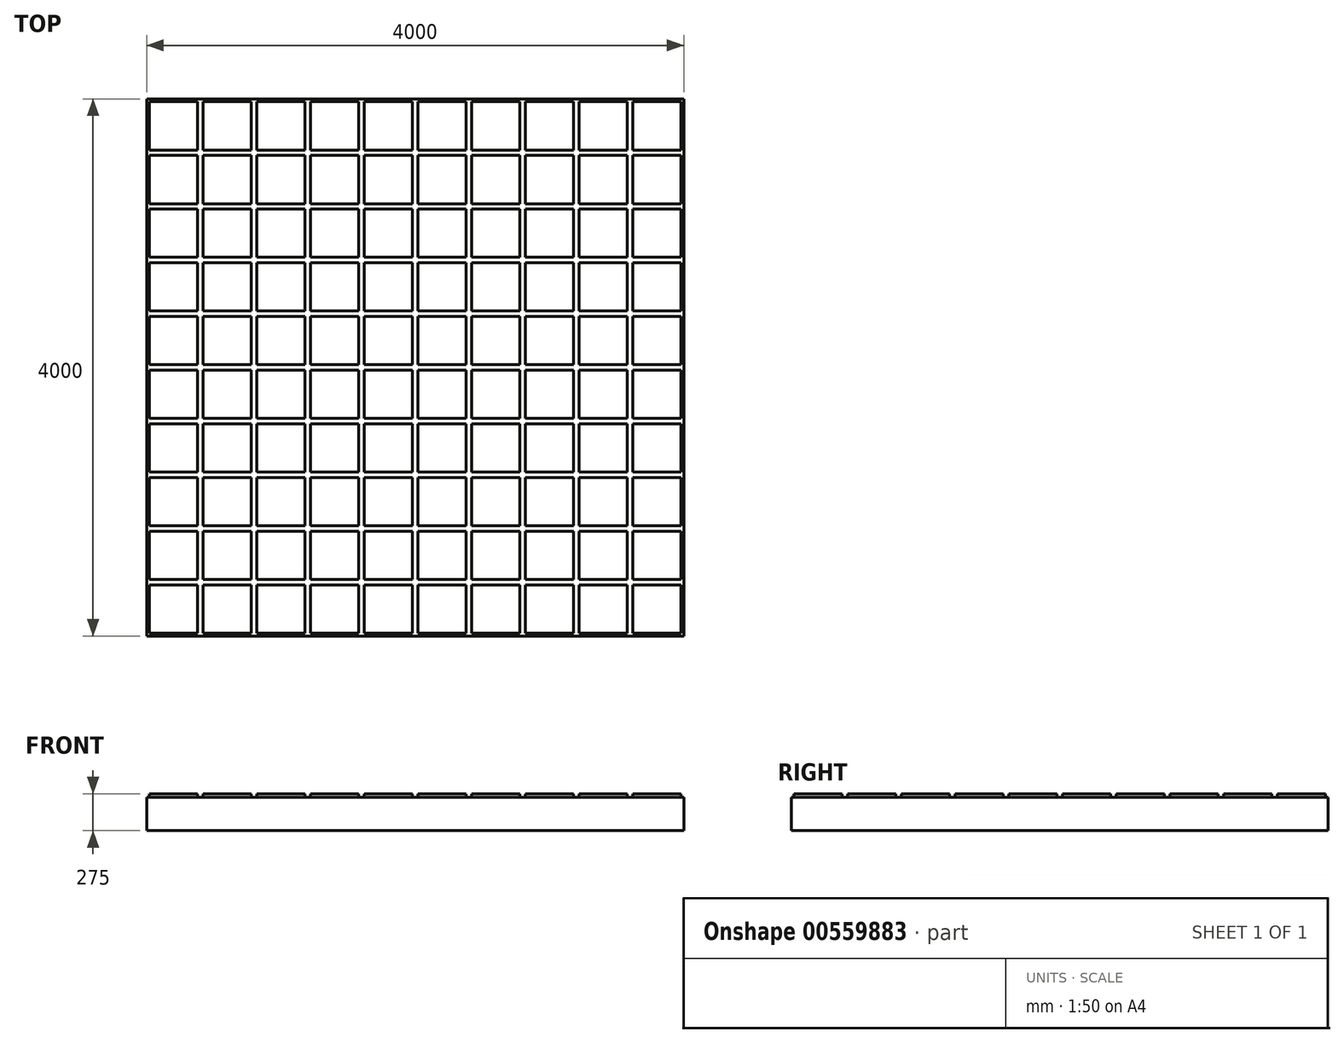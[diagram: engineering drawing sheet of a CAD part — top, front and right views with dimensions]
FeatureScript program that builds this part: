
annotation { "Feature Type Name" : "Feature", "Feature Type Description" : "" }
export const myFeature = defineFeature(function(context is Context, id is Id, definition is map)
    precondition{}
    {
        {
            var Q0;
            Q0=qCreatedBy(makeId("Top.planeOp"),FACE);
            var sketch = newSketch(context, id + "F0", { "sketchPlane" : qUnion([Q0])});
            skLineSegment(sketch, "E0.bottom", {"start": v(2000, 2000) * mm, "end": v(-2000, 2000) * mm});
            skLineSegment(sketch, "E0.top", {"start": v(2000, -2000) * mm, "end": v(-2000, -2000) * mm});
            skLineSegment(sketch, "E0.left", {"start": v(2000, 2000) * mm, "end": v(2000, -2000) * mm});
            skLineSegment(sketch, "E0.right", {"start": v(-2000, 2000) * mm, "end": v(-2000, -2000) * mm});
            skPoint(sketch, "E0.middle", {"position": v(0, 0) * mm});
            skSolve(sketch);
        }
        {
            var Q0;
            Q0 = qSketchRegion(id + "F0", true);
            extrude(context, id + "F1", {"entities" : qUnion([Q0]), "depth" : 250 * mm, "offsetDistance" : 25 * mm});
        }
        {
            var Q0;
            Q0=makeQuery(id+"F1.opExtrude","CAP_FACE",FACE,{"disambiguationData":[OSD([sQuery(id+"F0.wireOp",EDGE,"E0.bottom"),sQuery(id+"F0.wireOp",EDGE,"E0.top"),sQuery(id+"F0.wireOp",EDGE,"E0.left"),sQuery(id+"F0.wireOp",EDGE,"E0.right")])],"isStart":false});
            var sketch = newSketch(context, id + "F2", { "sketchPlane" : qUnion([Q0])});
            skLineSegment(sketch, "E1.bottom", {"start": v(-1620, 1620) * mm, "end": v(-1980, 1620) * mm});
            skLineSegment(sketch, "E1.top", {"start": v(-1620, 1980) * mm, "end": v(-1980, 1980) * mm});
            skLineSegment(sketch, "E1.left", {"start": v(-1620, 1620) * mm, "end": v(-1620, 1980) * mm});
            skLineSegment(sketch, "E1.right", {"start": v(-1980, 1620) * mm, "end": v(-1980, 1980) * mm});
            skPoint(sketch, "E1.middle", {"position": v(-1800, 1800) * mm});
            skLineSegment(sketch, "E2.0.1.0", {"start": v(-1620, 1580) * mm, "end": v(-1980, 1580) * mm});
            skLineSegment(sketch, "E2.0.1.1", {"start": v(-1980, 1220) * mm, "end": v(-1980, 1580) * mm});
            skLineSegment(sketch, "E2.0.1.2", {"start": v(-1620, 1220) * mm, "end": v(-1620, 1580) * mm});
            skLineSegment(sketch, "E2.0.1.3", {"start": v(-1620, 1220) * mm, "end": v(-1980, 1220) * mm});
            skLineSegment(sketch, "E2.0.2.0", {"start": v(-1620, 1180) * mm, "end": v(-1980, 1180) * mm});
            skLineSegment(sketch, "E2.0.2.1", {"start": v(-1980, 820) * mm, "end": v(-1980, 1180) * mm});
            skLineSegment(sketch, "E2.0.2.2", {"start": v(-1620, 820) * mm, "end": v(-1620, 1180) * mm});
            skLineSegment(sketch, "E2.0.2.3", {"start": v(-1620, 820) * mm, "end": v(-1980, 820) * mm});
            skLineSegment(sketch, "E2.0.3.0", {"start": v(-1620, 780) * mm, "end": v(-1980, 780) * mm});
            skLineSegment(sketch, "E2.0.3.1", {"start": v(-1980, 420) * mm, "end": v(-1980, 780) * mm});
            skLineSegment(sketch, "E2.0.3.2", {"start": v(-1620, 420) * mm, "end": v(-1620, 780) * mm});
            skLineSegment(sketch, "E2.0.3.3", {"start": v(-1620, 420) * mm, "end": v(-1980, 420) * mm});
            skLineSegment(sketch, "E2.0.4.0", {"start": v(-1620, 380) * mm, "end": v(-1980, 380) * mm});
            skLineSegment(sketch, "E2.0.4.1", {"start": v(-1980, 20) * mm, "end": v(-1980, 380) * mm});
            skLineSegment(sketch, "E2.0.4.2", {"start": v(-1620, 20) * mm, "end": v(-1620, 380) * mm});
            skLineSegment(sketch, "E2.0.4.3", {"start": v(-1620, 20) * mm, "end": v(-1980, 20) * mm});
            skLineSegment(sketch, "E2.0.5.0", {"start": v(-1620, -20) * mm, "end": v(-1980, -20) * mm});
            skLineSegment(sketch, "E2.0.5.1", {"start": v(-1980, -380) * mm, "end": v(-1980, -20) * mm});
            skLineSegment(sketch, "E2.0.5.2", {"start": v(-1620, -380) * mm, "end": v(-1620, -20) * mm});
            skLineSegment(sketch, "E2.0.5.3", {"start": v(-1620, -380) * mm, "end": v(-1980, -380) * mm});
            skLineSegment(sketch, "E2.0.6.0", {"start": v(-1620, -420) * mm, "end": v(-1980, -420) * mm});
            skLineSegment(sketch, "E2.0.6.1", {"start": v(-1980, -780) * mm, "end": v(-1980, -420) * mm});
            skLineSegment(sketch, "E2.0.6.2", {"start": v(-1620, -780) * mm, "end": v(-1620, -420) * mm});
            skLineSegment(sketch, "E2.0.6.3", {"start": v(-1620, -780) * mm, "end": v(-1980, -780) * mm});
            skLineSegment(sketch, "E2.0.7.0", {"start": v(-1620, -820) * mm, "end": v(-1980, -820) * mm});
            skLineSegment(sketch, "E2.0.7.1", {"start": v(-1980, -1180) * mm, "end": v(-1980, -820) * mm});
            skLineSegment(sketch, "E2.0.7.2", {"start": v(-1620, -1180) * mm, "end": v(-1620, -820) * mm});
            skLineSegment(sketch, "E2.0.7.3", {"start": v(-1620, -1180) * mm, "end": v(-1980, -1180) * mm});
            skLineSegment(sketch, "E2.0.8.0", {"start": v(-1620, -1220) * mm, "end": v(-1980, -1220) * mm});
            skLineSegment(sketch, "E2.0.8.1", {"start": v(-1980, -1580) * mm, "end": v(-1980, -1220) * mm});
            skLineSegment(sketch, "E2.0.8.2", {"start": v(-1620, -1580) * mm, "end": v(-1620, -1220) * mm});
            skLineSegment(sketch, "E2.0.8.3", {"start": v(-1620, -1580) * mm, "end": v(-1980, -1580) * mm});
            skLineSegment(sketch, "E2.0.9.0", {"start": v(-1620, -1620) * mm, "end": v(-1980, -1620) * mm});
            skLineSegment(sketch, "E2.0.9.1", {"start": v(-1980, -1980) * mm, "end": v(-1980, -1620) * mm});
            skLineSegment(sketch, "E2.0.9.2", {"start": v(-1620, -1980) * mm, "end": v(-1620, -1620) * mm});
            skLineSegment(sketch, "E2.0.9.3", {"start": v(-1620, -1980) * mm, "end": v(-1980, -1980) * mm});
            skLineSegment(sketch, "E2.1.0.0", {"start": v(-1220, 1980) * mm, "end": v(-1580, 1980) * mm});
            skLineSegment(sketch, "E2.1.0.1", {"start": v(-1580, 1620) * mm, "end": v(-1580, 1980) * mm});
            skLineSegment(sketch, "E2.1.0.2", {"start": v(-1220, 1620) * mm, "end": v(-1220, 1980) * mm});
            skLineSegment(sketch, "E2.1.0.3", {"start": v(-1220, 1620) * mm, "end": v(-1580, 1620) * mm});
            skLineSegment(sketch, "E2.1.1.0", {"start": v(-1220, 1580) * mm, "end": v(-1580, 1580) * mm});
            skLineSegment(sketch, "E2.1.1.1", {"start": v(-1580, 1220) * mm, "end": v(-1580, 1580) * mm});
            skLineSegment(sketch, "E2.1.1.2", {"start": v(-1220, 1220) * mm, "end": v(-1220, 1580) * mm});
            skLineSegment(sketch, "E2.1.1.3", {"start": v(-1220, 1220) * mm, "end": v(-1580, 1220) * mm});
            skLineSegment(sketch, "E2.1.2.0", {"start": v(-1220, 1180) * mm, "end": v(-1580, 1180) * mm});
            skLineSegment(sketch, "E2.1.2.1", {"start": v(-1580, 820) * mm, "end": v(-1580, 1180) * mm});
            skLineSegment(sketch, "E2.1.2.2", {"start": v(-1220, 820) * mm, "end": v(-1220, 1180) * mm});
            skLineSegment(sketch, "E2.1.2.3", {"start": v(-1220, 820) * mm, "end": v(-1580, 820) * mm});
            skLineSegment(sketch, "E2.1.3.0", {"start": v(-1220, 780) * mm, "end": v(-1580, 780) * mm});
            skLineSegment(sketch, "E2.1.3.1", {"start": v(-1580, 420) * mm, "end": v(-1580, 780) * mm});
            skLineSegment(sketch, "E2.1.3.2", {"start": v(-1220, 420) * mm, "end": v(-1220, 780) * mm});
            skLineSegment(sketch, "E2.1.3.3", {"start": v(-1220, 420) * mm, "end": v(-1580, 420) * mm});
            skLineSegment(sketch, "E2.1.4.0", {"start": v(-1220, 380) * mm, "end": v(-1580, 380) * mm});
            skLineSegment(sketch, "E2.1.4.1", {"start": v(-1580, 20) * mm, "end": v(-1580, 380) * mm});
            skLineSegment(sketch, "E2.1.4.2", {"start": v(-1220, 20) * mm, "end": v(-1220, 380) * mm});
            skLineSegment(sketch, "E2.1.4.3", {"start": v(-1220, 20) * mm, "end": v(-1580, 20) * mm});
            skLineSegment(sketch, "E2.1.5.0", {"start": v(-1220, -20) * mm, "end": v(-1580, -20) * mm});
            skLineSegment(sketch, "E2.1.5.1", {"start": v(-1580, -380) * mm, "end": v(-1580, -20) * mm});
            skLineSegment(sketch, "E2.1.5.2", {"start": v(-1220, -380) * mm, "end": v(-1220, -20) * mm});
            skLineSegment(sketch, "E2.1.5.3", {"start": v(-1220, -380) * mm, "end": v(-1580, -380) * mm});
            skLineSegment(sketch, "E2.1.6.0", {"start": v(-1220, -420) * mm, "end": v(-1580, -420) * mm});
            skLineSegment(sketch, "E2.1.6.1", {"start": v(-1580, -780) * mm, "end": v(-1580, -420) * mm});
            skLineSegment(sketch, "E2.1.6.2", {"start": v(-1220, -780) * mm, "end": v(-1220, -420) * mm});
            skLineSegment(sketch, "E2.1.6.3", {"start": v(-1220, -780) * mm, "end": v(-1580, -780) * mm});
            skLineSegment(sketch, "E2.1.7.0", {"start": v(-1220, -820) * mm, "end": v(-1580, -820) * mm});
            skLineSegment(sketch, "E2.1.7.1", {"start": v(-1580, -1180) * mm, "end": v(-1580, -820) * mm});
            skLineSegment(sketch, "E2.1.7.2", {"start": v(-1220, -1180) * mm, "end": v(-1220, -820) * mm});
            skLineSegment(sketch, "E2.1.7.3", {"start": v(-1220, -1180) * mm, "end": v(-1580, -1180) * mm});
            skLineSegment(sketch, "E2.1.8.0", {"start": v(-1220, -1220) * mm, "end": v(-1580, -1220) * mm});
            skLineSegment(sketch, "E2.1.8.1", {"start": v(-1580, -1580) * mm, "end": v(-1580, -1220) * mm});
            skLineSegment(sketch, "E2.1.8.2", {"start": v(-1220, -1580) * mm, "end": v(-1220, -1220) * mm});
            skLineSegment(sketch, "E2.1.8.3", {"start": v(-1220, -1580) * mm, "end": v(-1580, -1580) * mm});
            skLineSegment(sketch, "E2.1.9.0", {"start": v(-1220, -1620) * mm, "end": v(-1580, -1620) * mm});
            skLineSegment(sketch, "E2.1.9.1", {"start": v(-1580, -1980) * mm, "end": v(-1580, -1620) * mm});
            skLineSegment(sketch, "E2.1.9.2", {"start": v(-1220, -1980) * mm, "end": v(-1220, -1620) * mm});
            skLineSegment(sketch, "E2.1.9.3", {"start": v(-1220, -1980) * mm, "end": v(-1580, -1980) * mm});
            skLineSegment(sketch, "E2.2.0.0", {"start": v(-820, 1980) * mm, "end": v(-1180, 1980) * mm});
            skLineSegment(sketch, "E2.2.0.1", {"start": v(-1180, 1620) * mm, "end": v(-1180, 1980) * mm});
            skLineSegment(sketch, "E2.2.0.2", {"start": v(-820, 1620) * mm, "end": v(-820, 1980) * mm});
            skLineSegment(sketch, "E2.2.0.3", {"start": v(-820, 1620) * mm, "end": v(-1180, 1620) * mm});
            skLineSegment(sketch, "E2.2.1.0", {"start": v(-820, 1580) * mm, "end": v(-1180, 1580) * mm});
            skLineSegment(sketch, "E2.2.1.1", {"start": v(-1180, 1220) * mm, "end": v(-1180, 1580) * mm});
            skLineSegment(sketch, "E2.2.1.2", {"start": v(-820, 1220) * mm, "end": v(-820, 1580) * mm});
            skLineSegment(sketch, "E2.2.1.3", {"start": v(-820, 1220) * mm, "end": v(-1180, 1220) * mm});
            skLineSegment(sketch, "E2.2.2.0", {"start": v(-820, 1180) * mm, "end": v(-1180, 1180) * mm});
            skLineSegment(sketch, "E2.2.2.1", {"start": v(-1180, 820) * mm, "end": v(-1180, 1180) * mm});
            skLineSegment(sketch, "E2.2.2.2", {"start": v(-820, 820) * mm, "end": v(-820, 1180) * mm});
            skLineSegment(sketch, "E2.2.2.3", {"start": v(-820, 820) * mm, "end": v(-1180, 820) * mm});
            skLineSegment(sketch, "E2.2.3.0", {"start": v(-820, 780) * mm, "end": v(-1180, 780) * mm});
            skLineSegment(sketch, "E2.2.3.1", {"start": v(-1180, 420) * mm, "end": v(-1180, 780) * mm});
            skLineSegment(sketch, "E2.2.3.2", {"start": v(-820, 420) * mm, "end": v(-820, 780) * mm});
            skLineSegment(sketch, "E2.2.3.3", {"start": v(-820, 420) * mm, "end": v(-1180, 420) * mm});
            skLineSegment(sketch, "E2.2.4.0", {"start": v(-820, 380) * mm, "end": v(-1180, 380) * mm});
            skLineSegment(sketch, "E2.2.4.1", {"start": v(-1180, 20) * mm, "end": v(-1180, 380) * mm});
            skLineSegment(sketch, "E2.2.4.2", {"start": v(-820, 20) * mm, "end": v(-820, 380) * mm});
            skLineSegment(sketch, "E2.2.4.3", {"start": v(-820, 20) * mm, "end": v(-1180, 20) * mm});
            skLineSegment(sketch, "E2.2.5.0", {"start": v(-820, -20) * mm, "end": v(-1180, -20) * mm});
            skLineSegment(sketch, "E2.2.5.1", {"start": v(-1180, -380) * mm, "end": v(-1180, -20) * mm});
            skLineSegment(sketch, "E2.2.5.2", {"start": v(-820, -380) * mm, "end": v(-820, -20) * mm});
            skLineSegment(sketch, "E2.2.5.3", {"start": v(-820, -380) * mm, "end": v(-1180, -380) * mm});
            skLineSegment(sketch, "E2.2.6.0", {"start": v(-820, -420) * mm, "end": v(-1180, -420) * mm});
            skLineSegment(sketch, "E2.2.6.1", {"start": v(-1180, -780) * mm, "end": v(-1180, -420) * mm});
            skLineSegment(sketch, "E2.2.6.2", {"start": v(-820, -780) * mm, "end": v(-820, -420) * mm});
            skLineSegment(sketch, "E2.2.6.3", {"start": v(-820, -780) * mm, "end": v(-1180, -780) * mm});
            skLineSegment(sketch, "E2.2.7.0", {"start": v(-820, -820) * mm, "end": v(-1180, -820) * mm});
            skLineSegment(sketch, "E2.2.7.1", {"start": v(-1180, -1180) * mm, "end": v(-1180, -820) * mm});
            skLineSegment(sketch, "E2.2.7.2", {"start": v(-820, -1180) * mm, "end": v(-820, -820) * mm});
            skLineSegment(sketch, "E2.2.7.3", {"start": v(-820, -1180) * mm, "end": v(-1180, -1180) * mm});
            skLineSegment(sketch, "E2.2.8.0", {"start": v(-820, -1220) * mm, "end": v(-1180, -1220) * mm});
            skLineSegment(sketch, "E2.2.8.1", {"start": v(-1180, -1580) * mm, "end": v(-1180, -1220) * mm});
            skLineSegment(sketch, "E2.2.8.2", {"start": v(-820, -1580) * mm, "end": v(-820, -1220) * mm});
            skLineSegment(sketch, "E2.2.8.3", {"start": v(-820, -1580) * mm, "end": v(-1180, -1580) * mm});
            skLineSegment(sketch, "E2.2.9.0", {"start": v(-820, -1620) * mm, "end": v(-1180, -1620) * mm});
            skLineSegment(sketch, "E2.2.9.1", {"start": v(-1180, -1980) * mm, "end": v(-1180, -1620) * mm});
            skLineSegment(sketch, "E2.2.9.2", {"start": v(-820, -1980) * mm, "end": v(-820, -1620) * mm});
            skLineSegment(sketch, "E2.2.9.3", {"start": v(-820, -1980) * mm, "end": v(-1180, -1980) * mm});
            skLineSegment(sketch, "E2.3.0.0", {"start": v(-420, 1980) * mm, "end": v(-780, 1980) * mm});
            skLineSegment(sketch, "E2.3.0.1", {"start": v(-780, 1620) * mm, "end": v(-780, 1980) * mm});
            skLineSegment(sketch, "E2.3.0.2", {"start": v(-420, 1620) * mm, "end": v(-420, 1980) * mm});
            skLineSegment(sketch, "E2.3.0.3", {"start": v(-420, 1620) * mm, "end": v(-780, 1620) * mm});
            skLineSegment(sketch, "E2.3.1.0", {"start": v(-420, 1580) * mm, "end": v(-780, 1580) * mm});
            skLineSegment(sketch, "E2.3.1.1", {"start": v(-780, 1220) * mm, "end": v(-780, 1580) * mm});
            skLineSegment(sketch, "E2.3.1.2", {"start": v(-420, 1220) * mm, "end": v(-420, 1580) * mm});
            skLineSegment(sketch, "E2.3.1.3", {"start": v(-420, 1220) * mm, "end": v(-780, 1220) * mm});
            skLineSegment(sketch, "E2.3.2.0", {"start": v(-420, 1180) * mm, "end": v(-780, 1180) * mm});
            skLineSegment(sketch, "E2.3.2.1", {"start": v(-780, 820) * mm, "end": v(-780, 1180) * mm});
            skLineSegment(sketch, "E2.3.2.2", {"start": v(-420, 820) * mm, "end": v(-420, 1180) * mm});
            skLineSegment(sketch, "E2.3.2.3", {"start": v(-420, 820) * mm, "end": v(-780, 820) * mm});
            skLineSegment(sketch, "E2.3.3.0", {"start": v(-420, 780) * mm, "end": v(-780, 780) * mm});
            skLineSegment(sketch, "E2.3.3.1", {"start": v(-780, 420) * mm, "end": v(-780, 780) * mm});
            skLineSegment(sketch, "E2.3.3.2", {"start": v(-420, 420) * mm, "end": v(-420, 780) * mm});
            skLineSegment(sketch, "E2.3.3.3", {"start": v(-420, 420) * mm, "end": v(-780, 420) * mm});
            skLineSegment(sketch, "E2.3.4.0", {"start": v(-420, 380) * mm, "end": v(-780, 380) * mm});
            skLineSegment(sketch, "E2.3.4.1", {"start": v(-780, 20) * mm, "end": v(-780, 380) * mm});
            skLineSegment(sketch, "E2.3.4.2", {"start": v(-420, 20) * mm, "end": v(-420, 380) * mm});
            skLineSegment(sketch, "E2.3.4.3", {"start": v(-420, 20) * mm, "end": v(-780, 20) * mm});
            skLineSegment(sketch, "E2.3.5.0", {"start": v(-420, -20) * mm, "end": v(-780, -20) * mm});
            skLineSegment(sketch, "E2.3.5.1", {"start": v(-780, -380) * mm, "end": v(-780, -20) * mm});
            skLineSegment(sketch, "E2.3.5.2", {"start": v(-420, -380) * mm, "end": v(-420, -20) * mm});
            skLineSegment(sketch, "E2.3.5.3", {"start": v(-420, -380) * mm, "end": v(-780, -380) * mm});
            skLineSegment(sketch, "E2.3.6.0", {"start": v(-420, -420) * mm, "end": v(-780, -420) * mm});
            skLineSegment(sketch, "E2.3.6.1", {"start": v(-780, -780) * mm, "end": v(-780, -420) * mm});
            skLineSegment(sketch, "E2.3.6.2", {"start": v(-420, -780) * mm, "end": v(-420, -420) * mm});
            skLineSegment(sketch, "E2.3.6.3", {"start": v(-420, -780) * mm, "end": v(-780, -780) * mm});
            skLineSegment(sketch, "E2.3.7.0", {"start": v(-420, -820) * mm, "end": v(-780, -820) * mm});
            skLineSegment(sketch, "E2.3.7.1", {"start": v(-780, -1180) * mm, "end": v(-780, -820) * mm});
            skLineSegment(sketch, "E2.3.7.2", {"start": v(-420, -1180) * mm, "end": v(-420, -820) * mm});
            skLineSegment(sketch, "E2.3.7.3", {"start": v(-420, -1180) * mm, "end": v(-780, -1180) * mm});
            skLineSegment(sketch, "E2.3.8.0", {"start": v(-420, -1220) * mm, "end": v(-780, -1220) * mm});
            skLineSegment(sketch, "E2.3.8.1", {"start": v(-780, -1580) * mm, "end": v(-780, -1220) * mm});
            skLineSegment(sketch, "E2.3.8.2", {"start": v(-420, -1580) * mm, "end": v(-420, -1220) * mm});
            skLineSegment(sketch, "E2.3.8.3", {"start": v(-420, -1580) * mm, "end": v(-780, -1580) * mm});
            skLineSegment(sketch, "E2.3.9.0", {"start": v(-420, -1620) * mm, "end": v(-780, -1620) * mm});
            skLineSegment(sketch, "E2.3.9.1", {"start": v(-780, -1980) * mm, "end": v(-780, -1620) * mm});
            skLineSegment(sketch, "E2.3.9.2", {"start": v(-420, -1980) * mm, "end": v(-420, -1620) * mm});
            skLineSegment(sketch, "E2.3.9.3", {"start": v(-420, -1980) * mm, "end": v(-780, -1980) * mm});
            skLineSegment(sketch, "E2.4.0.0", {"start": v(-20, 1980) * mm, "end": v(-380, 1980) * mm});
            skLineSegment(sketch, "E2.4.0.1", {"start": v(-380, 1620) * mm, "end": v(-380, 1980) * mm});
            skLineSegment(sketch, "E2.4.0.2", {"start": v(-20, 1620) * mm, "end": v(-20, 1980) * mm});
            skLineSegment(sketch, "E2.4.0.3", {"start": v(-20, 1620) * mm, "end": v(-380, 1620) * mm});
            skLineSegment(sketch, "E2.4.1.0", {"start": v(-20, 1580) * mm, "end": v(-380, 1580) * mm});
            skLineSegment(sketch, "E2.4.1.1", {"start": v(-380, 1220) * mm, "end": v(-380, 1580) * mm});
            skLineSegment(sketch, "E2.4.1.2", {"start": v(-20, 1220) * mm, "end": v(-20, 1580) * mm});
            skLineSegment(sketch, "E2.4.1.3", {"start": v(-20, 1220) * mm, "end": v(-380, 1220) * mm});
            skLineSegment(sketch, "E2.4.2.0", {"start": v(-20, 1180) * mm, "end": v(-380, 1180) * mm});
            skLineSegment(sketch, "E2.4.2.1", {"start": v(-380, 820) * mm, "end": v(-380, 1180) * mm});
            skLineSegment(sketch, "E2.4.2.2", {"start": v(-20, 820) * mm, "end": v(-20, 1180) * mm});
            skLineSegment(sketch, "E2.4.2.3", {"start": v(-20, 820) * mm, "end": v(-380, 820) * mm});
            skLineSegment(sketch, "E2.4.3.0", {"start": v(-20, 780) * mm, "end": v(-380, 780) * mm});
            skLineSegment(sketch, "E2.4.3.1", {"start": v(-380, 420) * mm, "end": v(-380, 780) * mm});
            skLineSegment(sketch, "E2.4.3.2", {"start": v(-20, 420) * mm, "end": v(-20, 780) * mm});
            skLineSegment(sketch, "E2.4.3.3", {"start": v(-20, 420) * mm, "end": v(-380, 420) * mm});
            skLineSegment(sketch, "E2.4.4.0", {"start": v(-20, 380) * mm, "end": v(-380, 380) * mm});
            skLineSegment(sketch, "E2.4.4.1", {"start": v(-380, 20) * mm, "end": v(-380, 380) * mm});
            skLineSegment(sketch, "E2.4.4.2", {"start": v(-20, 20) * mm, "end": v(-20, 380) * mm});
            skLineSegment(sketch, "E2.4.4.3", {"start": v(-20, 20) * mm, "end": v(-380, 20) * mm});
            skLineSegment(sketch, "E2.4.5.0", {"start": v(-20, -20) * mm, "end": v(-380, -20) * mm});
            skLineSegment(sketch, "E2.4.5.1", {"start": v(-380, -380) * mm, "end": v(-380, -20) * mm});
            skLineSegment(sketch, "E2.4.5.2", {"start": v(-20, -380) * mm, "end": v(-20, -20) * mm});
            skLineSegment(sketch, "E2.4.5.3", {"start": v(-20, -380) * mm, "end": v(-380, -380) * mm});
            skLineSegment(sketch, "E2.4.6.0", {"start": v(-20, -420) * mm, "end": v(-380, -420) * mm});
            skLineSegment(sketch, "E2.4.6.1", {"start": v(-380, -780) * mm, "end": v(-380, -420) * mm});
            skLineSegment(sketch, "E2.4.6.2", {"start": v(-20, -780) * mm, "end": v(-20, -420) * mm});
            skLineSegment(sketch, "E2.4.6.3", {"start": v(-20, -780) * mm, "end": v(-380, -780) * mm});
            skLineSegment(sketch, "E2.4.7.0", {"start": v(-20, -820) * mm, "end": v(-380, -820) * mm});
            skLineSegment(sketch, "E2.4.7.1", {"start": v(-380, -1180) * mm, "end": v(-380, -820) * mm});
            skLineSegment(sketch, "E2.4.7.2", {"start": v(-20, -1180) * mm, "end": v(-20, -820) * mm});
            skLineSegment(sketch, "E2.4.7.3", {"start": v(-20, -1180) * mm, "end": v(-380, -1180) * mm});
            skLineSegment(sketch, "E2.4.8.0", {"start": v(-20, -1220) * mm, "end": v(-380, -1220) * mm});
            skLineSegment(sketch, "E2.4.8.1", {"start": v(-380, -1580) * mm, "end": v(-380, -1220) * mm});
            skLineSegment(sketch, "E2.4.8.2", {"start": v(-20, -1580) * mm, "end": v(-20, -1220) * mm});
            skLineSegment(sketch, "E2.4.8.3", {"start": v(-20, -1580) * mm, "end": v(-380, -1580) * mm});
            skLineSegment(sketch, "E2.4.9.0", {"start": v(-20, -1620) * mm, "end": v(-380, -1620) * mm});
            skLineSegment(sketch, "E2.4.9.1", {"start": v(-380, -1980) * mm, "end": v(-380, -1620) * mm});
            skLineSegment(sketch, "E2.4.9.2", {"start": v(-20, -1980) * mm, "end": v(-20, -1620) * mm});
            skLineSegment(sketch, "E2.4.9.3", {"start": v(-20, -1980) * mm, "end": v(-380, -1980) * mm});
            skLineSegment(sketch, "E2.5.0.0", {"start": v(380, 1980) * mm, "end": v(20, 1980) * mm});
            skLineSegment(sketch, "E2.5.0.1", {"start": v(20, 1620) * mm, "end": v(20, 1980) * mm});
            skLineSegment(sketch, "E2.5.0.2", {"start": v(380, 1620) * mm, "end": v(380, 1980) * mm});
            skLineSegment(sketch, "E2.5.0.3", {"start": v(380, 1620) * mm, "end": v(20, 1620) * mm});
            skLineSegment(sketch, "E2.5.1.0", {"start": v(380, 1580) * mm, "end": v(20, 1580) * mm});
            skLineSegment(sketch, "E2.5.1.1", {"start": v(20, 1220) * mm, "end": v(20, 1580) * mm});
            skLineSegment(sketch, "E2.5.1.2", {"start": v(380, 1220) * mm, "end": v(380, 1580) * mm});
            skLineSegment(sketch, "E2.5.1.3", {"start": v(380, 1220) * mm, "end": v(20, 1220) * mm});
            skLineSegment(sketch, "E2.5.2.0", {"start": v(380, 1180) * mm, "end": v(20, 1180) * mm});
            skLineSegment(sketch, "E2.5.2.1", {"start": v(20, 820) * mm, "end": v(20, 1180) * mm});
            skLineSegment(sketch, "E2.5.2.2", {"start": v(380, 820) * mm, "end": v(380, 1180) * mm});
            skLineSegment(sketch, "E2.5.2.3", {"start": v(380, 820) * mm, "end": v(20, 820) * mm});
            skLineSegment(sketch, "E2.5.3.0", {"start": v(380, 780) * mm, "end": v(20, 780) * mm});
            skLineSegment(sketch, "E2.5.3.1", {"start": v(20, 420) * mm, "end": v(20, 780) * mm});
            skLineSegment(sketch, "E2.5.3.2", {"start": v(380, 420) * mm, "end": v(380, 780) * mm});
            skLineSegment(sketch, "E2.5.3.3", {"start": v(380, 420) * mm, "end": v(20, 420) * mm});
            skLineSegment(sketch, "E2.5.4.0", {"start": v(380, 380) * mm, "end": v(20, 380) * mm});
            skLineSegment(sketch, "E2.5.4.1", {"start": v(20, 20) * mm, "end": v(20, 380) * mm});
            skLineSegment(sketch, "E2.5.4.2", {"start": v(380, 20) * mm, "end": v(380, 380) * mm});
            skLineSegment(sketch, "E2.5.4.3", {"start": v(380, 20) * mm, "end": v(20, 20) * mm});
            skLineSegment(sketch, "E2.5.5.0", {"start": v(380, -20) * mm, "end": v(20, -20) * mm});
            skLineSegment(sketch, "E2.5.5.1", {"start": v(20, -380) * mm, "end": v(20, -20) * mm});
            skLineSegment(sketch, "E2.5.5.2", {"start": v(380, -380) * mm, "end": v(380, -20) * mm});
            skLineSegment(sketch, "E2.5.5.3", {"start": v(380, -380) * mm, "end": v(20, -380) * mm});
            skLineSegment(sketch, "E2.5.6.0", {"start": v(380, -420) * mm, "end": v(20, -420) * mm});
            skLineSegment(sketch, "E2.5.6.1", {"start": v(20, -780) * mm, "end": v(20, -420) * mm});
            skLineSegment(sketch, "E2.5.6.2", {"start": v(380, -780) * mm, "end": v(380, -420) * mm});
            skLineSegment(sketch, "E2.5.6.3", {"start": v(380, -780) * mm, "end": v(20, -780) * mm});
            skLineSegment(sketch, "E2.5.7.0", {"start": v(380, -820) * mm, "end": v(20, -820) * mm});
            skLineSegment(sketch, "E2.5.7.1", {"start": v(20, -1180) * mm, "end": v(20, -820) * mm});
            skLineSegment(sketch, "E2.5.7.2", {"start": v(380, -1180) * mm, "end": v(380, -820) * mm});
            skLineSegment(sketch, "E2.5.7.3", {"start": v(380, -1180) * mm, "end": v(20, -1180) * mm});
            skLineSegment(sketch, "E2.5.8.0", {"start": v(380, -1220) * mm, "end": v(20, -1220) * mm});
            skLineSegment(sketch, "E2.5.8.1", {"start": v(20, -1580) * mm, "end": v(20, -1220) * mm});
            skLineSegment(sketch, "E2.5.8.2", {"start": v(380, -1580) * mm, "end": v(380, -1220) * mm});
            skLineSegment(sketch, "E2.5.8.3", {"start": v(380, -1580) * mm, "end": v(20, -1580) * mm});
            skLineSegment(sketch, "E2.5.9.0", {"start": v(380, -1620) * mm, "end": v(20, -1620) * mm});
            skLineSegment(sketch, "E2.5.9.1", {"start": v(20, -1980) * mm, "end": v(20, -1620) * mm});
            skLineSegment(sketch, "E2.5.9.2", {"start": v(380, -1980) * mm, "end": v(380, -1620) * mm});
            skLineSegment(sketch, "E2.5.9.3", {"start": v(380, -1980) * mm, "end": v(20, -1980) * mm});
            skLineSegment(sketch, "E2.6.0.0", {"start": v(780, 1980) * mm, "end": v(420, 1980) * mm});
            skLineSegment(sketch, "E2.6.0.1", {"start": v(420, 1620) * mm, "end": v(420, 1980) * mm});
            skLineSegment(sketch, "E2.6.0.2", {"start": v(780, 1620) * mm, "end": v(780, 1980) * mm});
            skLineSegment(sketch, "E2.6.0.3", {"start": v(780, 1620) * mm, "end": v(420, 1620) * mm});
            skLineSegment(sketch, "E2.6.1.0", {"start": v(780, 1580) * mm, "end": v(420, 1580) * mm});
            skLineSegment(sketch, "E2.6.1.1", {"start": v(420, 1220) * mm, "end": v(420, 1580) * mm});
            skLineSegment(sketch, "E2.6.1.2", {"start": v(780, 1220) * mm, "end": v(780, 1580) * mm});
            skLineSegment(sketch, "E2.6.1.3", {"start": v(780, 1220) * mm, "end": v(420, 1220) * mm});
            skLineSegment(sketch, "E2.6.2.0", {"start": v(780, 1180) * mm, "end": v(420, 1180) * mm});
            skLineSegment(sketch, "E2.6.2.1", {"start": v(420, 820) * mm, "end": v(420, 1180) * mm});
            skLineSegment(sketch, "E2.6.2.2", {"start": v(780, 820) * mm, "end": v(780, 1180) * mm});
            skLineSegment(sketch, "E2.6.2.3", {"start": v(780, 820) * mm, "end": v(420, 820) * mm});
            skLineSegment(sketch, "E2.6.3.0", {"start": v(780, 780) * mm, "end": v(420, 780) * mm});
            skLineSegment(sketch, "E2.6.3.1", {"start": v(420, 420) * mm, "end": v(420, 780) * mm});
            skLineSegment(sketch, "E2.6.3.2", {"start": v(780, 420) * mm, "end": v(780, 780) * mm});
            skLineSegment(sketch, "E2.6.3.3", {"start": v(780, 420) * mm, "end": v(420, 420) * mm});
            skLineSegment(sketch, "E2.6.4.0", {"start": v(780, 380) * mm, "end": v(420, 380) * mm});
            skLineSegment(sketch, "E2.6.4.1", {"start": v(420, 20) * mm, "end": v(420, 380) * mm});
            skLineSegment(sketch, "E2.6.4.2", {"start": v(780, 20) * mm, "end": v(780, 380) * mm});
            skLineSegment(sketch, "E2.6.4.3", {"start": v(780, 20) * mm, "end": v(420, 20) * mm});
            skLineSegment(sketch, "E2.6.5.0", {"start": v(780, -20) * mm, "end": v(420, -20) * mm});
            skLineSegment(sketch, "E2.6.5.1", {"start": v(420, -380) * mm, "end": v(420, -20) * mm});
            skLineSegment(sketch, "E2.6.5.2", {"start": v(780, -380) * mm, "end": v(780, -20) * mm});
            skLineSegment(sketch, "E2.6.5.3", {"start": v(780, -380) * mm, "end": v(420, -380) * mm});
            skLineSegment(sketch, "E2.6.6.0", {"start": v(780, -420) * mm, "end": v(420, -420) * mm});
            skLineSegment(sketch, "E2.6.6.1", {"start": v(420, -780) * mm, "end": v(420, -420) * mm});
            skLineSegment(sketch, "E2.6.6.2", {"start": v(780, -780) * mm, "end": v(780, -420) * mm});
            skLineSegment(sketch, "E2.6.6.3", {"start": v(780, -780) * mm, "end": v(420, -780) * mm});
            skLineSegment(sketch, "E2.6.7.0", {"start": v(780, -820) * mm, "end": v(420, -820) * mm});
            skLineSegment(sketch, "E2.6.7.1", {"start": v(420, -1180) * mm, "end": v(420, -820) * mm});
            skLineSegment(sketch, "E2.6.7.2", {"start": v(780, -1180) * mm, "end": v(780, -820) * mm});
            skLineSegment(sketch, "E2.6.7.3", {"start": v(780, -1180) * mm, "end": v(420, -1180) * mm});
            skLineSegment(sketch, "E2.6.8.0", {"start": v(780, -1220) * mm, "end": v(420, -1220) * mm});
            skLineSegment(sketch, "E2.6.8.1", {"start": v(420, -1580) * mm, "end": v(420, -1220) * mm});
            skLineSegment(sketch, "E2.6.8.2", {"start": v(780, -1580) * mm, "end": v(780, -1220) * mm});
            skLineSegment(sketch, "E2.6.8.3", {"start": v(780, -1580) * mm, "end": v(420, -1580) * mm});
            skLineSegment(sketch, "E2.6.9.0", {"start": v(780, -1620) * mm, "end": v(420, -1620) * mm});
            skLineSegment(sketch, "E2.6.9.1", {"start": v(420, -1980) * mm, "end": v(420, -1620) * mm});
            skLineSegment(sketch, "E2.6.9.2", {"start": v(780, -1980) * mm, "end": v(780, -1620) * mm});
            skLineSegment(sketch, "E2.6.9.3", {"start": v(780, -1980) * mm, "end": v(420, -1980) * mm});
            skLineSegment(sketch, "E2.7.0.0", {"start": v(1180, 1980) * mm, "end": v(820, 1980) * mm});
            skLineSegment(sketch, "E2.7.0.1", {"start": v(820, 1620) * mm, "end": v(820, 1980) * mm});
            skLineSegment(sketch, "E2.7.0.2", {"start": v(1180, 1620) * mm, "end": v(1180, 1980) * mm});
            skLineSegment(sketch, "E2.7.0.3", {"start": v(1180, 1620) * mm, "end": v(820, 1620) * mm});
            skLineSegment(sketch, "E2.7.1.0", {"start": v(1180, 1580) * mm, "end": v(820, 1580) * mm});
            skLineSegment(sketch, "E2.7.1.1", {"start": v(820, 1220) * mm, "end": v(820, 1580) * mm});
            skLineSegment(sketch, "E2.7.1.2", {"start": v(1180, 1220) * mm, "end": v(1180, 1580) * mm});
            skLineSegment(sketch, "E2.7.1.3", {"start": v(1180, 1220) * mm, "end": v(820, 1220) * mm});
            skLineSegment(sketch, "E2.7.2.0", {"start": v(1180, 1180) * mm, "end": v(820, 1180) * mm});
            skLineSegment(sketch, "E2.7.2.1", {"start": v(820, 820) * mm, "end": v(820, 1180) * mm});
            skLineSegment(sketch, "E2.7.2.2", {"start": v(1180, 820) * mm, "end": v(1180, 1180) * mm});
            skLineSegment(sketch, "E2.7.2.3", {"start": v(1180, 820) * mm, "end": v(820, 820) * mm});
            skLineSegment(sketch, "E2.7.3.0", {"start": v(1180, 780) * mm, "end": v(820, 780) * mm});
            skLineSegment(sketch, "E2.7.3.1", {"start": v(820, 420) * mm, "end": v(820, 780) * mm});
            skLineSegment(sketch, "E2.7.3.2", {"start": v(1180, 420) * mm, "end": v(1180, 780) * mm});
            skLineSegment(sketch, "E2.7.3.3", {"start": v(1180, 420) * mm, "end": v(820, 420) * mm});
            skLineSegment(sketch, "E2.7.4.0", {"start": v(1180, 380) * mm, "end": v(820, 380) * mm});
            skLineSegment(sketch, "E2.7.4.1", {"start": v(820, 20) * mm, "end": v(820, 380) * mm});
            skLineSegment(sketch, "E2.7.4.2", {"start": v(1180, 20) * mm, "end": v(1180, 380) * mm});
            skLineSegment(sketch, "E2.7.4.3", {"start": v(1180, 20) * mm, "end": v(820, 20) * mm});
            skLineSegment(sketch, "E2.7.5.0", {"start": v(1180, -20) * mm, "end": v(820, -20) * mm});
            skLineSegment(sketch, "E2.7.5.1", {"start": v(820, -380) * mm, "end": v(820, -20) * mm});
            skLineSegment(sketch, "E2.7.5.2", {"start": v(1180, -380) * mm, "end": v(1180, -20) * mm});
            skLineSegment(sketch, "E2.7.5.3", {"start": v(1180, -380) * mm, "end": v(820, -380) * mm});
            skLineSegment(sketch, "E2.7.6.0", {"start": v(1180, -420) * mm, "end": v(820, -420) * mm});
            skLineSegment(sketch, "E2.7.6.1", {"start": v(820, -780) * mm, "end": v(820, -420) * mm});
            skLineSegment(sketch, "E2.7.6.2", {"start": v(1180, -780) * mm, "end": v(1180, -420) * mm});
            skLineSegment(sketch, "E2.7.6.3", {"start": v(1180, -780) * mm, "end": v(820, -780) * mm});
            skLineSegment(sketch, "E2.7.7.0", {"start": v(1180, -820) * mm, "end": v(820, -820) * mm});
            skLineSegment(sketch, "E2.7.7.1", {"start": v(820, -1180) * mm, "end": v(820, -820) * mm});
            skLineSegment(sketch, "E2.7.7.2", {"start": v(1180, -1180) * mm, "end": v(1180, -820) * mm});
            skLineSegment(sketch, "E2.7.7.3", {"start": v(1180, -1180) * mm, "end": v(820, -1180) * mm});
            skLineSegment(sketch, "E2.7.8.0", {"start": v(1180, -1220) * mm, "end": v(820, -1220) * mm});
            skLineSegment(sketch, "E2.7.8.1", {"start": v(820, -1580) * mm, "end": v(820, -1220) * mm});
            skLineSegment(sketch, "E2.7.8.2", {"start": v(1180, -1580) * mm, "end": v(1180, -1220) * mm});
            skLineSegment(sketch, "E2.7.8.3", {"start": v(1180, -1580) * mm, "end": v(820, -1580) * mm});
            skLineSegment(sketch, "E2.7.9.0", {"start": v(1180, -1620) * mm, "end": v(820, -1620) * mm});
            skLineSegment(sketch, "E2.7.9.1", {"start": v(820, -1980) * mm, "end": v(820, -1620) * mm});
            skLineSegment(sketch, "E2.7.9.2", {"start": v(1180, -1980) * mm, "end": v(1180, -1620) * mm});
            skLineSegment(sketch, "E2.7.9.3", {"start": v(1180, -1980) * mm, "end": v(820, -1980) * mm});
            skLineSegment(sketch, "E2.8.0.0", {"start": v(1580, 1980) * mm, "end": v(1220, 1980) * mm});
            skLineSegment(sketch, "E2.8.0.1", {"start": v(1220, 1620) * mm, "end": v(1220, 1980) * mm});
            skLineSegment(sketch, "E2.8.0.2", {"start": v(1580, 1620) * mm, "end": v(1580, 1980) * mm});
            skLineSegment(sketch, "E2.8.0.3", {"start": v(1580, 1620) * mm, "end": v(1220, 1620) * mm});
            skLineSegment(sketch, "E2.8.1.0", {"start": v(1580, 1580) * mm, "end": v(1220, 1580) * mm});
            skLineSegment(sketch, "E2.8.1.1", {"start": v(1220, 1220) * mm, "end": v(1220, 1580) * mm});
            skLineSegment(sketch, "E2.8.1.2", {"start": v(1580, 1220) * mm, "end": v(1580, 1580) * mm});
            skLineSegment(sketch, "E2.8.1.3", {"start": v(1580, 1220) * mm, "end": v(1220, 1220) * mm});
            skLineSegment(sketch, "E2.8.2.0", {"start": v(1580, 1180) * mm, "end": v(1220, 1180) * mm});
            skLineSegment(sketch, "E2.8.2.1", {"start": v(1220, 820) * mm, "end": v(1220, 1180) * mm});
            skLineSegment(sketch, "E2.8.2.2", {"start": v(1580, 820) * mm, "end": v(1580, 1180) * mm});
            skLineSegment(sketch, "E2.8.2.3", {"start": v(1580, 820) * mm, "end": v(1220, 820) * mm});
            skLineSegment(sketch, "E2.8.3.0", {"start": v(1580, 780) * mm, "end": v(1220, 780) * mm});
            skLineSegment(sketch, "E2.8.3.1", {"start": v(1220, 420) * mm, "end": v(1220, 780) * mm});
            skLineSegment(sketch, "E2.8.3.2", {"start": v(1580, 420) * mm, "end": v(1580, 780) * mm});
            skLineSegment(sketch, "E2.8.3.3", {"start": v(1580, 420) * mm, "end": v(1220, 420) * mm});
            skLineSegment(sketch, "E2.8.4.0", {"start": v(1580, 380) * mm, "end": v(1220, 380) * mm});
            skLineSegment(sketch, "E2.8.4.1", {"start": v(1220, 20) * mm, "end": v(1220, 380) * mm});
            skLineSegment(sketch, "E2.8.4.2", {"start": v(1580, 20) * mm, "end": v(1580, 380) * mm});
            skLineSegment(sketch, "E2.8.4.3", {"start": v(1580, 20) * mm, "end": v(1220, 20) * mm});
            skLineSegment(sketch, "E2.8.5.0", {"start": v(1580, -20) * mm, "end": v(1220, -20) * mm});
            skLineSegment(sketch, "E2.8.5.1", {"start": v(1220, -380) * mm, "end": v(1220, -20) * mm});
            skLineSegment(sketch, "E2.8.5.2", {"start": v(1580, -380) * mm, "end": v(1580, -20) * mm});
            skLineSegment(sketch, "E2.8.5.3", {"start": v(1580, -380) * mm, "end": v(1220, -380) * mm});
            skLineSegment(sketch, "E2.8.6.0", {"start": v(1580, -420) * mm, "end": v(1220, -420) * mm});
            skLineSegment(sketch, "E2.8.6.1", {"start": v(1220, -780) * mm, "end": v(1220, -420) * mm});
            skLineSegment(sketch, "E2.8.6.2", {"start": v(1580, -780) * mm, "end": v(1580, -420) * mm});
            skLineSegment(sketch, "E2.8.6.3", {"start": v(1580, -780) * mm, "end": v(1220, -780) * mm});
            skLineSegment(sketch, "E2.8.7.0", {"start": v(1580, -820) * mm, "end": v(1220, -820) * mm});
            skLineSegment(sketch, "E2.8.7.1", {"start": v(1220, -1180) * mm, "end": v(1220, -820) * mm});
            skLineSegment(sketch, "E2.8.7.2", {"start": v(1580, -1180) * mm, "end": v(1580, -820) * mm});
            skLineSegment(sketch, "E2.8.7.3", {"start": v(1580, -1180) * mm, "end": v(1220, -1180) * mm});
            skLineSegment(sketch, "E2.8.8.0", {"start": v(1580, -1220) * mm, "end": v(1220, -1220) * mm});
            skLineSegment(sketch, "E2.8.8.1", {"start": v(1220, -1580) * mm, "end": v(1220, -1220) * mm});
            skLineSegment(sketch, "E2.8.8.2", {"start": v(1580, -1580) * mm, "end": v(1580, -1220) * mm});
            skLineSegment(sketch, "E2.8.8.3", {"start": v(1580, -1580) * mm, "end": v(1220, -1580) * mm});
            skLineSegment(sketch, "E2.8.9.0", {"start": v(1580, -1620) * mm, "end": v(1220, -1620) * mm});
            skLineSegment(sketch, "E2.8.9.1", {"start": v(1220, -1980) * mm, "end": v(1220, -1620) * mm});
            skLineSegment(sketch, "E2.8.9.2", {"start": v(1580, -1980) * mm, "end": v(1580, -1620) * mm});
            skLineSegment(sketch, "E2.8.9.3", {"start": v(1580, -1980) * mm, "end": v(1220, -1980) * mm});
            skLineSegment(sketch, "E2.9.0.0", {"start": v(1980, 1980) * mm, "end": v(1620, 1980) * mm});
            skLineSegment(sketch, "E2.9.0.1", {"start": v(1620, 1620) * mm, "end": v(1620, 1980) * mm});
            skLineSegment(sketch, "E2.9.0.2", {"start": v(1980, 1620) * mm, "end": v(1980, 1980) * mm});
            skLineSegment(sketch, "E2.9.0.3", {"start": v(1980, 1620) * mm, "end": v(1620, 1620) * mm});
            skLineSegment(sketch, "E2.9.1.0", {"start": v(1980, 1580) * mm, "end": v(1620, 1580) * mm});
            skLineSegment(sketch, "E2.9.1.1", {"start": v(1620, 1220) * mm, "end": v(1620, 1580) * mm});
            skLineSegment(sketch, "E2.9.1.2", {"start": v(1980, 1220) * mm, "end": v(1980, 1580) * mm});
            skLineSegment(sketch, "E2.9.1.3", {"start": v(1980, 1220) * mm, "end": v(1620, 1220) * mm});
            skLineSegment(sketch, "E2.9.2.0", {"start": v(1980, 1180) * mm, "end": v(1620, 1180) * mm});
            skLineSegment(sketch, "E2.9.2.1", {"start": v(1620, 820) * mm, "end": v(1620, 1180) * mm});
            skLineSegment(sketch, "E2.9.2.2", {"start": v(1980, 820) * mm, "end": v(1980, 1180) * mm});
            skLineSegment(sketch, "E2.9.2.3", {"start": v(1980, 820) * mm, "end": v(1620, 820) * mm});
            skLineSegment(sketch, "E2.9.3.0", {"start": v(1980, 780) * mm, "end": v(1620, 780) * mm});
            skLineSegment(sketch, "E2.9.3.1", {"start": v(1620, 420) * mm, "end": v(1620, 780) * mm});
            skLineSegment(sketch, "E2.9.3.2", {"start": v(1980, 420) * mm, "end": v(1980, 780) * mm});
            skLineSegment(sketch, "E2.9.3.3", {"start": v(1980, 420) * mm, "end": v(1620, 420) * mm});
            skLineSegment(sketch, "E2.9.4.0", {"start": v(1980, 380) * mm, "end": v(1620, 380) * mm});
            skLineSegment(sketch, "E2.9.4.1", {"start": v(1620, 20) * mm, "end": v(1620, 380) * mm});
            skLineSegment(sketch, "E2.9.4.2", {"start": v(1980, 20) * mm, "end": v(1980, 380) * mm});
            skLineSegment(sketch, "E2.9.4.3", {"start": v(1980, 20) * mm, "end": v(1620, 20) * mm});
            skLineSegment(sketch, "E2.9.5.0", {"start": v(1980, -20) * mm, "end": v(1620, -20) * mm});
            skLineSegment(sketch, "E2.9.5.1", {"start": v(1620, -380) * mm, "end": v(1620, -20) * mm});
            skLineSegment(sketch, "E2.9.5.2", {"start": v(1980, -380) * mm, "end": v(1980, -20) * mm});
            skLineSegment(sketch, "E2.9.5.3", {"start": v(1980, -380) * mm, "end": v(1620, -380) * mm});
            skLineSegment(sketch, "E2.9.6.0", {"start": v(1980, -420) * mm, "end": v(1620, -420) * mm});
            skLineSegment(sketch, "E2.9.6.1", {"start": v(1620, -780) * mm, "end": v(1620, -420) * mm});
            skLineSegment(sketch, "E2.9.6.2", {"start": v(1980, -780) * mm, "end": v(1980, -420) * mm});
            skLineSegment(sketch, "E2.9.6.3", {"start": v(1980, -780) * mm, "end": v(1620, -780) * mm});
            skLineSegment(sketch, "E2.9.7.0", {"start": v(1980, -820) * mm, "end": v(1620, -820) * mm});
            skLineSegment(sketch, "E2.9.7.1", {"start": v(1620, -1180) * mm, "end": v(1620, -820) * mm});
            skLineSegment(sketch, "E2.9.7.2", {"start": v(1980, -1180) * mm, "end": v(1980, -820) * mm});
            skLineSegment(sketch, "E2.9.7.3", {"start": v(1980, -1180) * mm, "end": v(1620, -1180) * mm});
            skLineSegment(sketch, "E2.9.8.0", {"start": v(1980, -1220) * mm, "end": v(1620, -1220) * mm});
            skLineSegment(sketch, "E2.9.8.1", {"start": v(1620, -1580) * mm, "end": v(1620, -1220) * mm});
            skLineSegment(sketch, "E2.9.8.2", {"start": v(1980, -1580) * mm, "end": v(1980, -1220) * mm});
            skLineSegment(sketch, "E2.9.8.3", {"start": v(1980, -1580) * mm, "end": v(1620, -1580) * mm});
            skLineSegment(sketch, "E2.9.9.0", {"start": v(1980, -1620) * mm, "end": v(1620, -1620) * mm});
            skLineSegment(sketch, "E2.9.9.1", {"start": v(1620, -1980) * mm, "end": v(1620, -1620) * mm});
            skLineSegment(sketch, "E2.9.9.2", {"start": v(1980, -1980) * mm, "end": v(1980, -1620) * mm});
            skLineSegment(sketch, "E2.9.9.3", {"start": v(1980, -1980) * mm, "end": v(1620, -1980) * mm});
            skLineSegment(sketch, "E2.direction1", {"start": v(-1980, 1620) * mm, "end": v(-1580, 1620) * mm, "construction": true});
            skLineSegment(sketch, "E2.direction2", {"start": v(-1980, 1620) * mm, "end": v(-1980, 1220) * mm, "construction": true});
            skSolve(sketch);
        }
        {
            var Q0;
            Q0=makeQuery(id+"F2.imprint","IMPRINT",FACE,{"disambiguationData":[TD([[makeQuery(id+"F2.imprint","IMPRINT",EDGE,{"derivedFrom":sQuery(id+"F2.wireOp",EDGE,"E1.bottom")}),-1.0]])]});
            var Q1;
            Q1=makeQuery(id+"F2.imprint","IMPRINT",FACE,{"disambiguationData":[TD([[makeQuery(id+"F2.imprint","IMPRINT",EDGE,{"derivedFrom":sQuery(id+"F2.wireOp",EDGE,"E2.1.0.0")}),1.0]])]});
            var Q2;
            Q2=makeQuery(id+"F2.imprint","IMPRINT",FACE,{"disambiguationData":[TD([[makeQuery(id+"F2.imprint","IMPRINT",EDGE,{"derivedFrom":sQuery(id+"F2.wireOp",EDGE,"E2.2.0.0")}),1.0]])]});
            var Q3;
            Q3=makeQuery(id+"F2.imprint","IMPRINT",FACE,{"disambiguationData":[TD([[makeQuery(id+"F2.imprint","IMPRINT",EDGE,{"derivedFrom":sQuery(id+"F2.wireOp",EDGE,"E2.3.0.0")}),1.0]])]});
            var Q4;
            Q4=makeQuery(id+"F2.imprint","IMPRINT",FACE,{"disambiguationData":[TD([[makeQuery(id+"F2.imprint","IMPRINT",EDGE,{"derivedFrom":sQuery(id+"F2.wireOp",EDGE,"E2.4.0.0")}),1.0]])]});
            var Q5;
            Q5=makeQuery(id+"F2.imprint","IMPRINT",FACE,{"disambiguationData":[TD([[makeQuery(id+"F2.imprint","IMPRINT",EDGE,{"derivedFrom":sQuery(id+"F2.wireOp",EDGE,"E2.5.0.0")}),1.0]])]});
            var Q6;
            Q6=makeQuery(id+"F2.imprint","IMPRINT",FACE,{"disambiguationData":[TD([[makeQuery(id+"F2.imprint","IMPRINT",EDGE,{"derivedFrom":sQuery(id+"F2.wireOp",EDGE,"E2.6.0.0")}),1.0]])]});
            var Q7;
            Q7=makeQuery(id+"F2.imprint","IMPRINT",FACE,{"disambiguationData":[TD([[makeQuery(id+"F2.imprint","IMPRINT",EDGE,{"derivedFrom":sQuery(id+"F2.wireOp",EDGE,"E2.7.0.0")}),1.0]])]});
            var Q8;
            Q8=makeQuery(id+"F2.imprint","IMPRINT",FACE,{"disambiguationData":[TD([[makeQuery(id+"F2.imprint","IMPRINT",EDGE,{"derivedFrom":sQuery(id+"F2.wireOp",EDGE,"E2.8.0.0")}),1.0]])]});
            var Q9;
            Q9=makeQuery(id+"F2.imprint","IMPRINT",FACE,{"disambiguationData":[TD([[makeQuery(id+"F2.imprint","IMPRINT",EDGE,{"derivedFrom":sQuery(id+"F2.wireOp",EDGE,"E2.9.0.0")}),1.0]])]});
            var Q10;
            Q10=makeQuery(id+"F2.imprint","IMPRINT",FACE,{"disambiguationData":[TD([[makeQuery(id+"F2.imprint","IMPRINT",EDGE,{"derivedFrom":sQuery(id+"F2.wireOp",EDGE,"E2.9.1.0")}),1.0]])]});
            var Q11;
            Q11=makeQuery(id+"F2.imprint","IMPRINT",FACE,{"disambiguationData":[TD([[makeQuery(id+"F2.imprint","IMPRINT",EDGE,{"derivedFrom":sQuery(id+"F2.wireOp",EDGE,"E2.7.1.0")}),1.0]])]});
            var Q12;
            Q12=makeQuery(id+"F2.imprint","IMPRINT",FACE,{"disambiguationData":[TD([[makeQuery(id+"F2.imprint","IMPRINT",EDGE,{"derivedFrom":sQuery(id+"F2.wireOp",EDGE,"E2.6.1.0")}),1.0]])]});
            var Q13;
            Q13=makeQuery(id+"F2.imprint","IMPRINT",FACE,{"disambiguationData":[TD([[makeQuery(id+"F2.imprint","IMPRINT",EDGE,{"derivedFrom":sQuery(id+"F2.wireOp",EDGE,"E2.5.1.0")}),1.0]])]});
            var Q14;
            Q14=makeQuery(id+"F2.imprint","IMPRINT",FACE,{"disambiguationData":[TD([[makeQuery(id+"F2.imprint","IMPRINT",EDGE,{"derivedFrom":sQuery(id+"F2.wireOp",EDGE,"E2.4.1.0")}),1.0]])]});
            var Q15;
            Q15=makeQuery(id+"F2.imprint","IMPRINT",FACE,{"disambiguationData":[TD([[makeQuery(id+"F2.imprint","IMPRINT",EDGE,{"derivedFrom":sQuery(id+"F2.wireOp",EDGE,"E2.3.1.0")}),1.0]])]});
            var Q16;
            Q16=makeQuery(id+"F2.imprint","IMPRINT",FACE,{"disambiguationData":[TD([[makeQuery(id+"F2.imprint","IMPRINT",EDGE,{"derivedFrom":sQuery(id+"F2.wireOp",EDGE,"E2.2.1.0")}),1.0]])]});
            var Q17;
            Q17=makeQuery(id+"F2.imprint","IMPRINT",FACE,{"disambiguationData":[TD([[makeQuery(id+"F2.imprint","IMPRINT",EDGE,{"derivedFrom":sQuery(id+"F2.wireOp",EDGE,"E2.1.1.0")}),1.0]])]});
            var Q18;
            Q18=makeQuery(id+"F2.imprint","IMPRINT",FACE,{"disambiguationData":[TD([[makeQuery(id+"F2.imprint","IMPRINT",EDGE,{"derivedFrom":sQuery(id+"F2.wireOp",EDGE,"E2.0.1.0")}),1.0]])]});
            var Q19;
            Q19=makeQuery(id+"F2.imprint","IMPRINT",FACE,{"disambiguationData":[TD([[makeQuery(id+"F2.imprint","IMPRINT",EDGE,{"derivedFrom":sQuery(id+"F2.wireOp",EDGE,"E2.0.2.0")}),1.0]])]});
            var Q20;
            Q20=makeQuery(id+"F2.imprint","IMPRINT",FACE,{"disambiguationData":[TD([[makeQuery(id+"F2.imprint","IMPRINT",EDGE,{"derivedFrom":sQuery(id+"F2.wireOp",EDGE,"E2.1.2.0")}),1.0]])]});
            var Q21;
            Q21=makeQuery(id+"F2.imprint","IMPRINT",FACE,{"disambiguationData":[TD([[makeQuery(id+"F2.imprint","IMPRINT",EDGE,{"derivedFrom":sQuery(id+"F2.wireOp",EDGE,"E2.2.2.0")}),1.0]])]});
            var Q22;
            Q22=makeQuery(id+"F2.imprint","IMPRINT",FACE,{"disambiguationData":[TD([[makeQuery(id+"F2.imprint","IMPRINT",EDGE,{"derivedFrom":sQuery(id+"F2.wireOp",EDGE,"E2.1.1.0")}),1.0]])]});
            var Q23;
            Q23=makeQuery(id+"F2.imprint","IMPRINT",FACE,{"disambiguationData":[TD([[makeQuery(id+"F2.imprint","IMPRINT",EDGE,{"derivedFrom":sQuery(id+"F2.wireOp",EDGE,"E2.3.2.0")}),1.0]])]});
            var Q24;
            Q24=makeQuery(id+"F2.imprint","IMPRINT",FACE,{"disambiguationData":[TD([[makeQuery(id+"F2.imprint","IMPRINT",EDGE,{"derivedFrom":sQuery(id+"F2.wireOp",EDGE,"E2.4.2.0")}),1.0]])]});
            var Q25;
            Q25=makeQuery(id+"F2.imprint","IMPRINT",FACE,{"disambiguationData":[TD([[makeQuery(id+"F2.imprint","IMPRINT",EDGE,{"derivedFrom":sQuery(id+"F2.wireOp",EDGE,"E2.5.2.0")}),1.0]])]});
            var Q26;
            Q26=makeQuery(id+"F2.imprint","IMPRINT",FACE,{"disambiguationData":[TD([[makeQuery(id+"F2.imprint","IMPRINT",EDGE,{"derivedFrom":sQuery(id+"F2.wireOp",EDGE,"E2.6.2.0")}),1.0]])]});
            var Q27;
            Q27=makeQuery(id+"F2.imprint","IMPRINT",FACE,{"disambiguationData":[TD([[makeQuery(id+"F2.imprint","IMPRINT",EDGE,{"derivedFrom":sQuery(id+"F2.wireOp",EDGE,"E2.7.2.0")}),1.0]])]});
            var Q28;
            Q28=makeQuery(id+"F2.imprint","IMPRINT",FACE,{"disambiguationData":[TD([[makeQuery(id+"F2.imprint","IMPRINT",EDGE,{"derivedFrom":sQuery(id+"F2.wireOp",EDGE,"E2.8.1.0")}),1.0]])]});
            var Q29;
            Q29=makeQuery(id+"F2.imprint","IMPRINT",FACE,{"disambiguationData":[TD([[makeQuery(id+"F2.imprint","IMPRINT",EDGE,{"derivedFrom":sQuery(id+"F2.wireOp",EDGE,"E2.8.2.0")}),1.0]])]});
            var Q30;
            Q30=makeQuery(id+"F2.imprint","IMPRINT",FACE,{"disambiguationData":[TD([[makeQuery(id+"F2.imprint","IMPRINT",EDGE,{"derivedFrom":sQuery(id+"F2.wireOp",EDGE,"E2.9.2.0")}),1.0]])]});
            var Q31;
            Q31=makeQuery(id+"F2.imprint","IMPRINT",FACE,{"disambiguationData":[TD([[makeQuery(id+"F2.imprint","IMPRINT",EDGE,{"derivedFrom":sQuery(id+"F2.wireOp",EDGE,"E2.9.3.0")}),1.0]])]});
            var Q32;
            Q32=makeQuery(id+"F2.imprint","IMPRINT",FACE,{"disambiguationData":[TD([[makeQuery(id+"F2.imprint","IMPRINT",EDGE,{"derivedFrom":sQuery(id+"F2.wireOp",EDGE,"E2.8.3.0")}),1.0]])]});
            var Q33;
            Q33=makeQuery(id+"F2.imprint","IMPRINT",FACE,{"disambiguationData":[TD([[makeQuery(id+"F2.imprint","IMPRINT",EDGE,{"derivedFrom":sQuery(id+"F2.wireOp",EDGE,"E2.7.3.0")}),1.0]])]});
            var Q34;
            Q34=makeQuery(id+"F2.imprint","IMPRINT",FACE,{"disambiguationData":[TD([[makeQuery(id+"F2.imprint","IMPRINT",EDGE,{"derivedFrom":sQuery(id+"F2.wireOp",EDGE,"E2.6.3.0")}),1.0]])]});
            var Q35;
            Q35=makeQuery(id+"F2.imprint","IMPRINT",FACE,{"disambiguationData":[TD([[makeQuery(id+"F2.imprint","IMPRINT",EDGE,{"derivedFrom":sQuery(id+"F2.wireOp",EDGE,"E2.5.3.0")}),1.0]])]});
            var Q36;
            Q36=makeQuery(id+"F2.imprint","IMPRINT",FACE,{"disambiguationData":[TD([[makeQuery(id+"F2.imprint","IMPRINT",EDGE,{"derivedFrom":sQuery(id+"F2.wireOp",EDGE,"E2.4.3.0")}),1.0]])]});
            var Q37;
            Q37=makeQuery(id+"F2.imprint","IMPRINT",FACE,{"disambiguationData":[TD([[makeQuery(id+"F2.imprint","IMPRINT",EDGE,{"derivedFrom":sQuery(id+"F2.wireOp",EDGE,"E2.3.3.0")}),1.0]])]});
            var Q38;
            Q38=makeQuery(id+"F2.imprint","IMPRINT",FACE,{"disambiguationData":[TD([[makeQuery(id+"F2.imprint","IMPRINT",EDGE,{"derivedFrom":sQuery(id+"F2.wireOp",EDGE,"E2.2.3.0")}),1.0]])]});
            var Q39;
            Q39=makeQuery(id+"F2.imprint","IMPRINT",FACE,{"disambiguationData":[TD([[makeQuery(id+"F2.imprint","IMPRINT",EDGE,{"derivedFrom":sQuery(id+"F2.wireOp",EDGE,"E2.1.3.0")}),1.0]])]});
            var Q40;
            Q40=makeQuery(id+"F2.imprint","IMPRINT",FACE,{"disambiguationData":[TD([[makeQuery(id+"F2.imprint","IMPRINT",EDGE,{"derivedFrom":sQuery(id+"F2.wireOp",EDGE,"E2.0.3.0")}),1.0]])]});
            var Q41;
            Q41=makeQuery(id+"F2.imprint","IMPRINT",FACE,{"disambiguationData":[TD([[makeQuery(id+"F2.imprint","IMPRINT",EDGE,{"derivedFrom":sQuery(id+"F2.wireOp",EDGE,"E2.0.4.0")}),1.0]])]});
            var Q42;
            Q42=makeQuery(id+"F2.imprint","IMPRINT",FACE,{"disambiguationData":[TD([[makeQuery(id+"F2.imprint","IMPRINT",EDGE,{"derivedFrom":sQuery(id+"F2.wireOp",EDGE,"E2.1.4.0")}),1.0]])]});
            var Q43;
            Q43=makeQuery(id+"F2.imprint","IMPRINT",FACE,{"disambiguationData":[TD([[makeQuery(id+"F2.imprint","IMPRINT",EDGE,{"derivedFrom":sQuery(id+"F2.wireOp",EDGE,"E2.2.4.0")}),1.0]])]});
            var Q44;
            Q44=makeQuery(id+"F2.imprint","IMPRINT",FACE,{"disambiguationData":[TD([[makeQuery(id+"F2.imprint","IMPRINT",EDGE,{"derivedFrom":sQuery(id+"F2.wireOp",EDGE,"E2.3.4.0")}),1.0]])]});
            var Q45;
            Q45=makeQuery(id+"F2.imprint","IMPRINT",FACE,{"disambiguationData":[TD([[makeQuery(id+"F2.imprint","IMPRINT",EDGE,{"derivedFrom":sQuery(id+"F2.wireOp",EDGE,"E2.4.4.0")}),1.0]])]});
            var Q46;
            Q46=makeQuery(id+"F2.imprint","IMPRINT",FACE,{"disambiguationData":[TD([[makeQuery(id+"F2.imprint","IMPRINT",EDGE,{"derivedFrom":sQuery(id+"F2.wireOp",EDGE,"E2.5.4.0")}),1.0]])]});
            var Q47;
            Q47=makeQuery(id+"F2.imprint","IMPRINT",FACE,{"disambiguationData":[TD([[makeQuery(id+"F2.imprint","IMPRINT",EDGE,{"derivedFrom":sQuery(id+"F2.wireOp",EDGE,"E2.6.4.0")}),1.0]])]});
            var Q48;
            Q48=makeQuery(id+"F2.imprint","IMPRINT",FACE,{"disambiguationData":[TD([[makeQuery(id+"F2.imprint","IMPRINT",EDGE,{"derivedFrom":sQuery(id+"F2.wireOp",EDGE,"E2.7.4.0")}),1.0]])]});
            var Q49;
            Q49=makeQuery(id+"F2.imprint","IMPRINT",FACE,{"disambiguationData":[TD([[makeQuery(id+"F2.imprint","IMPRINT",EDGE,{"derivedFrom":sQuery(id+"F2.wireOp",EDGE,"E2.8.4.0")}),1.0]])]});
            var Q50;
            Q50=makeQuery(id+"F2.imprint","IMPRINT",FACE,{"disambiguationData":[TD([[makeQuery(id+"F2.imprint","IMPRINT",EDGE,{"derivedFrom":sQuery(id+"F2.wireOp",EDGE,"E2.9.4.0")}),1.0]])]});
            var Q51;
            Q51=makeQuery(id+"F2.imprint","IMPRINT",FACE,{"disambiguationData":[TD([[makeQuery(id+"F2.imprint","IMPRINT",EDGE,{"derivedFrom":sQuery(id+"F2.wireOp",EDGE,"E2.4.3.0")}),1.0]])]});
            var Q52;
            Q52=makeQuery(id+"F2.imprint","IMPRINT",FACE,{"disambiguationData":[TD([[makeQuery(id+"F2.imprint","IMPRINT",EDGE,{"derivedFrom":sQuery(id+"F2.wireOp",EDGE,"E2.0.5.0")}),1.0]])]});
            var Q53;
            Q53=makeQuery(id+"F2.imprint","IMPRINT",FACE,{"disambiguationData":[TD([[makeQuery(id+"F2.imprint","IMPRINT",EDGE,{"derivedFrom":sQuery(id+"F2.wireOp",EDGE,"E2.0.4.0")}),1.0]])]});
            var Q54;
            Q54=makeQuery(id+"F2.imprint","IMPRINT",FACE,{"disambiguationData":[TD([[makeQuery(id+"F2.imprint","IMPRINT",EDGE,{"derivedFrom":sQuery(id+"F2.wireOp",EDGE,"E2.1.5.0")}),1.0]])]});
            var Q55;
            Q55=makeQuery(id+"F2.imprint","IMPRINT",FACE,{"disambiguationData":[TD([[makeQuery(id+"F2.imprint","IMPRINT",EDGE,{"derivedFrom":sQuery(id+"F2.wireOp",EDGE,"E2.2.5.0")}),1.0]])]});
            var Q56;
            Q56=makeQuery(id+"F2.imprint","IMPRINT",FACE,{"disambiguationData":[TD([[makeQuery(id+"F2.imprint","IMPRINT",EDGE,{"derivedFrom":sQuery(id+"F2.wireOp",EDGE,"E2.3.5.0")}),1.0]])]});
            var Q57;
            Q57=makeQuery(id+"F2.imprint","IMPRINT",FACE,{"disambiguationData":[TD([[makeQuery(id+"F2.imprint","IMPRINT",EDGE,{"derivedFrom":sQuery(id+"F2.wireOp",EDGE,"E2.4.5.0")}),1.0]])]});
            var Q58;
            Q58=makeQuery(id+"F2.imprint","IMPRINT",FACE,{"disambiguationData":[TD([[makeQuery(id+"F2.imprint","IMPRINT",EDGE,{"derivedFrom":sQuery(id+"F2.wireOp",EDGE,"E2.5.5.0")}),1.0]])]});
            var Q59;
            Q59=makeQuery(id+"F2.imprint","IMPRINT",FACE,{"disambiguationData":[TD([[makeQuery(id+"F2.imprint","IMPRINT",EDGE,{"derivedFrom":sQuery(id+"F2.wireOp",EDGE,"E2.6.5.0")}),1.0]])]});
            var Q60;
            Q60=makeQuery(id+"F2.imprint","IMPRINT",FACE,{"disambiguationData":[TD([[makeQuery(id+"F2.imprint","IMPRINT",EDGE,{"derivedFrom":sQuery(id+"F2.wireOp",EDGE,"E2.7.5.0")}),1.0]])]});
            var Q61;
            Q61=makeQuery(id+"F2.imprint","IMPRINT",FACE,{"disambiguationData":[TD([[makeQuery(id+"F2.imprint","IMPRINT",EDGE,{"derivedFrom":sQuery(id+"F2.wireOp",EDGE,"E2.8.5.0")}),1.0]])]});
            var Q62;
            Q62=makeQuery(id+"F2.imprint","IMPRINT",FACE,{"disambiguationData":[TD([[makeQuery(id+"F2.imprint","IMPRINT",EDGE,{"derivedFrom":sQuery(id+"F2.wireOp",EDGE,"E2.9.5.0")}),1.0]])]});
            var Q63;
            Q63=makeQuery(id+"F2.imprint","IMPRINT",FACE,{"disambiguationData":[TD([[makeQuery(id+"F2.imprint","IMPRINT",EDGE,{"derivedFrom":sQuery(id+"F2.wireOp",EDGE,"E2.9.6.0")}),1.0]])]});
            var Q64;
            Q64=makeQuery(id+"F2.imprint","IMPRINT",FACE,{"disambiguationData":[TD([[makeQuery(id+"F2.imprint","IMPRINT",EDGE,{"derivedFrom":sQuery(id+"F2.wireOp",EDGE,"E2.8.6.0")}),1.0]])]});
            var Q65;
            Q65=makeQuery(id+"F2.imprint","IMPRINT",FACE,{"disambiguationData":[TD([[makeQuery(id+"F2.imprint","IMPRINT",EDGE,{"derivedFrom":sQuery(id+"F2.wireOp",EDGE,"E2.7.6.0")}),1.0]])]});
            var Q66;
            Q66=makeQuery(id+"F2.imprint","IMPRINT",FACE,{"disambiguationData":[TD([[makeQuery(id+"F2.imprint","IMPRINT",EDGE,{"derivedFrom":sQuery(id+"F2.wireOp",EDGE,"E2.6.6.0")}),1.0]])]});
            var Q67;
            Q67=makeQuery(id+"F2.imprint","IMPRINT",FACE,{"disambiguationData":[TD([[makeQuery(id+"F2.imprint","IMPRINT",EDGE,{"derivedFrom":sQuery(id+"F2.wireOp",EDGE,"E2.5.6.0")}),1.0]])]});
            var Q68;
            Q68=makeQuery(id+"F2.imprint","IMPRINT",FACE,{"disambiguationData":[TD([[makeQuery(id+"F2.imprint","IMPRINT",EDGE,{"derivedFrom":sQuery(id+"F2.wireOp",EDGE,"E2.0.6.0")}),1.0]])]});
            var Q69;
            Q69=makeQuery(id+"F2.imprint","IMPRINT",FACE,{"disambiguationData":[TD([[makeQuery(id+"F2.imprint","IMPRINT",EDGE,{"derivedFrom":sQuery(id+"F2.wireOp",EDGE,"E2.1.6.0")}),1.0]])]});
            var Q70;
            Q70=makeQuery(id+"F2.imprint","IMPRINT",FACE,{"disambiguationData":[TD([[makeQuery(id+"F2.imprint","IMPRINT",EDGE,{"derivedFrom":sQuery(id+"F2.wireOp",EDGE,"E2.2.6.0")}),1.0]])]});
            var Q71;
            Q71=makeQuery(id+"F2.imprint","IMPRINT",FACE,{"disambiguationData":[TD([[makeQuery(id+"F2.imprint","IMPRINT",EDGE,{"derivedFrom":sQuery(id+"F2.wireOp",EDGE,"E2.3.6.0")}),1.0]])]});
            var Q72;
            Q72=makeQuery(id+"F2.imprint","IMPRINT",FACE,{"disambiguationData":[TD([[makeQuery(id+"F2.imprint","IMPRINT",EDGE,{"derivedFrom":sQuery(id+"F2.wireOp",EDGE,"E2.4.6.0")}),1.0]])]});
            var Q73;
            Q73=makeQuery(id+"F2.imprint","IMPRINT",FACE,{"disambiguationData":[TD([[makeQuery(id+"F2.imprint","IMPRINT",EDGE,{"derivedFrom":sQuery(id+"F2.wireOp",EDGE,"E2.0.7.0")}),1.0]])]});
            var Q74;
            Q74=makeQuery(id+"F2.imprint","IMPRINT",FACE,{"disambiguationData":[TD([[makeQuery(id+"F2.imprint","IMPRINT",EDGE,{"derivedFrom":sQuery(id+"F2.wireOp",EDGE,"E2.1.7.0")}),1.0]])]});
            var Q75;
            Q75=makeQuery(id+"F2.imprint","IMPRINT",FACE,{"disambiguationData":[TD([[makeQuery(id+"F2.imprint","IMPRINT",EDGE,{"derivedFrom":sQuery(id+"F2.wireOp",EDGE,"E2.2.7.0")}),1.0]])]});
            var Q76;
            Q76=makeQuery(id+"F2.imprint","IMPRINT",FACE,{"disambiguationData":[TD([[makeQuery(id+"F2.imprint","IMPRINT",EDGE,{"derivedFrom":sQuery(id+"F2.wireOp",EDGE,"E2.3.7.0")}),1.0]])]});
            var Q77;
            Q77=makeQuery(id+"F2.imprint","IMPRINT",FACE,{"disambiguationData":[TD([[makeQuery(id+"F2.imprint","IMPRINT",EDGE,{"derivedFrom":sQuery(id+"F2.wireOp",EDGE,"E2.4.7.0")}),1.0]])]});
            var Q78;
            Q78=makeQuery(id+"F2.imprint","IMPRINT",FACE,{"disambiguationData":[TD([[makeQuery(id+"F2.imprint","IMPRINT",EDGE,{"derivedFrom":sQuery(id+"F2.wireOp",EDGE,"E2.5.7.0")}),1.0]])]});
            var Q79;
            Q79=makeQuery(id+"F2.imprint","IMPRINT",FACE,{"disambiguationData":[TD([[makeQuery(id+"F2.imprint","IMPRINT",EDGE,{"derivedFrom":sQuery(id+"F2.wireOp",EDGE,"E2.6.7.0")}),1.0]])]});
            var Q80;
            Q80=makeQuery(id+"F2.imprint","IMPRINT",FACE,{"disambiguationData":[TD([[makeQuery(id+"F2.imprint","IMPRINT",EDGE,{"derivedFrom":sQuery(id+"F2.wireOp",EDGE,"E2.7.7.0")}),1.0]])]});
            var Q81;
            Q81=makeQuery(id+"F2.imprint","IMPRINT",FACE,{"disambiguationData":[TD([[makeQuery(id+"F2.imprint","IMPRINT",EDGE,{"derivedFrom":sQuery(id+"F2.wireOp",EDGE,"E2.8.7.0")}),1.0]])]});
            var Q82;
            Q82=makeQuery(id+"F2.imprint","IMPRINT",FACE,{"disambiguationData":[TD([[makeQuery(id+"F2.imprint","IMPRINT",EDGE,{"derivedFrom":sQuery(id+"F2.wireOp",EDGE,"E2.9.7.0")}),1.0]])]});
            var Q83;
            Q83=makeQuery(id+"F2.imprint","IMPRINT",FACE,{"disambiguationData":[TD([[makeQuery(id+"F2.imprint","IMPRINT",EDGE,{"derivedFrom":sQuery(id+"F2.wireOp",EDGE,"E2.9.8.0")}),1.0]])]});
            var Q84;
            Q84=makeQuery(id+"F2.imprint","IMPRINT",FACE,{"disambiguationData":[TD([[makeQuery(id+"F2.imprint","IMPRINT",EDGE,{"derivedFrom":sQuery(id+"F2.wireOp",EDGE,"E2.8.8.0")}),1.0]])]});
            var Q85;
            Q85=makeQuery(id+"F2.imprint","IMPRINT",FACE,{"disambiguationData":[TD([[makeQuery(id+"F2.imprint","IMPRINT",EDGE,{"derivedFrom":sQuery(id+"F2.wireOp",EDGE,"E2.7.8.0")}),1.0]])]});
            var Q86;
            Q86=makeQuery(id+"F2.imprint","IMPRINT",FACE,{"disambiguationData":[TD([[makeQuery(id+"F2.imprint","IMPRINT",EDGE,{"derivedFrom":sQuery(id+"F2.wireOp",EDGE,"E2.6.8.0")}),1.0]])]});
            var Q87;
            Q87=makeQuery(id+"F2.imprint","IMPRINT",FACE,{"disambiguationData":[TD([[makeQuery(id+"F2.imprint","IMPRINT",EDGE,{"derivedFrom":sQuery(id+"F2.wireOp",EDGE,"E2.5.8.0")}),1.0]])]});
            var Q88;
            Q88=makeQuery(id+"F2.imprint","IMPRINT",FACE,{"disambiguationData":[TD([[makeQuery(id+"F2.imprint","IMPRINT",EDGE,{"derivedFrom":sQuery(id+"F2.wireOp",EDGE,"E2.4.8.0")}),1.0]])]});
            var Q89;
            Q89=makeQuery(id+"F2.imprint","IMPRINT",FACE,{"disambiguationData":[TD([[makeQuery(id+"F2.imprint","IMPRINT",EDGE,{"derivedFrom":sQuery(id+"F2.wireOp",EDGE,"E2.3.8.0")}),1.0]])]});
            var Q90;
            Q90=makeQuery(id+"F2.imprint","IMPRINT",FACE,{"disambiguationData":[TD([[makeQuery(id+"F2.imprint","IMPRINT",EDGE,{"derivedFrom":sQuery(id+"F2.wireOp",EDGE,"E2.2.8.0")}),1.0]])]});
            var Q91;
            Q91=makeQuery(id+"F2.imprint","IMPRINT",FACE,{"disambiguationData":[TD([[makeQuery(id+"F2.imprint","IMPRINT",EDGE,{"derivedFrom":sQuery(id+"F2.wireOp",EDGE,"E2.9.9.0")}),1.0]])]});
            var Q92;
            Q92=makeQuery(id+"F2.imprint","IMPRINT",FACE,{"disambiguationData":[TD([[makeQuery(id+"F2.imprint","IMPRINT",EDGE,{"derivedFrom":sQuery(id+"F2.wireOp",EDGE,"E2.8.9.0")}),1.0]])]});
            var Q93;
            Q93=makeQuery(id+"F2.imprint","IMPRINT",FACE,{"disambiguationData":[TD([[makeQuery(id+"F2.imprint","IMPRINT",EDGE,{"derivedFrom":sQuery(id+"F2.wireOp",EDGE,"E2.7.9.0")}),1.0]])]});
            var Q94;
            Q94=makeQuery(id+"F2.imprint","IMPRINT",FACE,{"disambiguationData":[TD([[makeQuery(id+"F2.imprint","IMPRINT",EDGE,{"derivedFrom":sQuery(id+"F2.wireOp",EDGE,"E2.6.9.0")}),1.0]])]});
            var Q95;
            Q95=makeQuery(id+"F2.imprint","IMPRINT",FACE,{"disambiguationData":[TD([[makeQuery(id+"F2.imprint","IMPRINT",EDGE,{"derivedFrom":sQuery(id+"F2.wireOp",EDGE,"E2.5.9.0")}),1.0]])]});
            var Q96;
            Q96=makeQuery(id+"F2.imprint","IMPRINT",FACE,{"disambiguationData":[TD([[makeQuery(id+"F2.imprint","IMPRINT",EDGE,{"derivedFrom":sQuery(id+"F2.wireOp",EDGE,"E2.0.8.0")}),1.0]])]});
            var Q97;
            Q97=makeQuery(id+"F2.imprint","IMPRINT",FACE,{"disambiguationData":[TD([[makeQuery(id+"F2.imprint","IMPRINT",EDGE,{"derivedFrom":sQuery(id+"F2.wireOp",EDGE,"E2.1.8.0")}),1.0]])]});
            var Q98;
            Q98=makeQuery(id+"F2.imprint","IMPRINT",FACE,{"disambiguationData":[TD([[makeQuery(id+"F2.imprint","IMPRINT",EDGE,{"derivedFrom":sQuery(id+"F2.wireOp",EDGE,"E2.0.9.0")}),1.0]])]});
            var Q99;
            Q99=makeQuery(id+"F2.imprint","IMPRINT",FACE,{"disambiguationData":[TD([[makeQuery(id+"F2.imprint","IMPRINT",EDGE,{"derivedFrom":sQuery(id+"F2.wireOp",EDGE,"E2.1.9.0")}),1.0]])]});
            var Q100;
            Q100=makeQuery(id+"F2.imprint","IMPRINT",FACE,{"disambiguationData":[TD([[makeQuery(id+"F2.imprint","IMPRINT",EDGE,{"derivedFrom":sQuery(id+"F2.wireOp",EDGE,"E2.2.9.0")}),1.0]])]});
            var Q101;
            Q101=makeQuery(id+"F2.imprint","IMPRINT",FACE,{"disambiguationData":[TD([[makeQuery(id+"F2.imprint","IMPRINT",EDGE,{"derivedFrom":sQuery(id+"F2.wireOp",EDGE,"E2.3.9.0")}),1.0]])]});
            var Q102;
            Q102=makeQuery(id+"F2.imprint","IMPRINT",FACE,{"disambiguationData":[TD([[makeQuery(id+"F2.imprint","IMPRINT",EDGE,{"derivedFrom":sQuery(id+"F2.wireOp",EDGE,"E2.4.9.0")}),1.0]])]});
            extrude(context, id + "F3", {"entities" : qUnion([Q0, Q1, Q2, Q3, Q4, Q5, Q6, Q7, Q8, Q9, Q10, Q11, Q12, Q13, Q14, Q15, Q16, Q17, Q18, Q19, Q20, Q21, Q22, Q23, Q24, Q25, Q26, Q27, Q28, Q29, Q30, Q31, Q32, Q33, Q34, Q35, Q36, Q37, Q38, Q39, Q40, Q41, Q42, Q43, Q44, Q45, Q46, Q47, Q48, Q49, Q50, Q51, Q52, Q53, Q54, Q55, Q56, Q57, Q58, Q59, Q60, Q61, Q62, Q63, Q64, Q65, Q66, Q67, Q68, Q69, Q70, Q71, Q72, Q73, Q74, Q75, Q76, Q77, Q78, Q79, Q80, Q81, Q82, Q83, Q84, Q85, Q86, Q87, Q88, Q89, Q90, Q91, Q92, Q93, Q94, Q95, Q96, Q97, Q98, Q99, Q100, Q101, Q102]), "operationType" : NewBodyOperationType.ADD, "depth" : 25 * mm, "offsetDistance" : 25 * mm});
        }
    });
